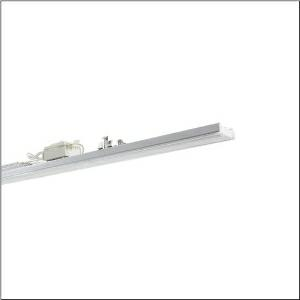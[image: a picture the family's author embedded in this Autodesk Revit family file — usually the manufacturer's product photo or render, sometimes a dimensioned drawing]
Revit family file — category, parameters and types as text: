
# Revit family: licross_21_recessed_ho_52tl12dn1e5m
name_source: partatom
category: Lighting Fixtures
units: mm (PartAtom-declared; Revit-internal decimal feet)

## family parameters
Cut with Voids When Loaded = No
Host = Face
Light Source = No
Part Type = Normal
Room Calculation Point = No
Round Connector Dimension = Use Diameter
Shared = No

## types (1)
- --- (1 x LED, 14510 lm, 84.6 W, 3500K)
    Apparent Load = 85 VA
    CIE Flux Codes = 69 91 98 100 100
    Color Rendering = 80
    Color Temperature = 3500K
    Default Elevation = 1800 mm
    Description = Licross 21 Recessed HO, luminaire insert, of sheet steel, galvanised, coil coated, white, length: 1.500mm, width: 66mm, height: 67mm, LED rated luminous flux: 14.510lm, light colour: 835, SDCM (Standard Deviation of Colour Matching)MacAdam ≤ 3 SDCM (initial), control gear: DALI 2, with plug, 5-pole, with phase selection, mains connection: 220..240V, AC, 50/60Hz, rated input power: 85W, internal wiring halogen-free, primary optical cover: cover, of PMMA, light emission: direct distribution, primary light characteristic: symmetric, protection rating (complete): IP40, insulation class (complete): insulation class I (protective earthing), certification: CE, ENEC, VDE, UKCA, protection symbol: D if used in an environment without relevant dust loads with corresponding accessories, impact resistance: IK06, permissible ambient temperature for indoor applications: -25..+30°C, corresponds to IFS (International Featured Standards) requirements for safety and quality in the food industry, reducing of maximum allowable ambient temperature of 5°C with ceiling mounting, LABS conformity tested according to VDMA 24364:2018-05, The light source and the operating device comply with the requirements of the Ecodesign Regulation (EU) 2019/2020 and are replaceable in accordance with this regulation, packaging unit: 1 piece
    Height = 58 mm
    Lamp = 1 x LED
    Lamp Light Flux = 14510 lm
    Lamp Power = 84.6 W
    Lamp count = 1
    Length = 1500 mm
    Luminous efficacy = 172 lm/W
    Manufacturer = Siteco
    ModVariant = No
    Model = 52TL12DN1E5M
    Mounting Place = Ceiling
    Mounting Type = Pendant
    Number of Poles = 1
    OnlyDefault = Yes
    Power Factor = 1
    Product Name = Licross 21 Recessed HO
    Product group = luminaire insert | ceiling pendant
    ProductGroupID = 901
    Protection Class = Protection class I
    Protection Degree = IP 40
    RLX_Detail_Level = 1
    RLX_Emergency_Light_Flux = 0 lm
    RLX_Emergency_Type = 0
    RLX_Emergency_Type_DB = No
    RlxData = <blob elided: 24961 chars, md5=68e851f7>
    Socket = socket
    Standby Power = 0 W
    System Light Flux = 14510 lm
    System Power = 85 W
    Type Comments = factory setting: luminous flux: 100 % | dim-lin: 254 | 484 mA
    Type Image = l_1296930.jpg
    URL = http://relux.com
    VarID = @adj_092909
    Voltage = 0 V
    Weight = 0.00 kg
    Width = 66 mm

## geometry (parser evidence)
native form markers: Blend x4, Sweep x10
no freeform markers — native parametric forms only
